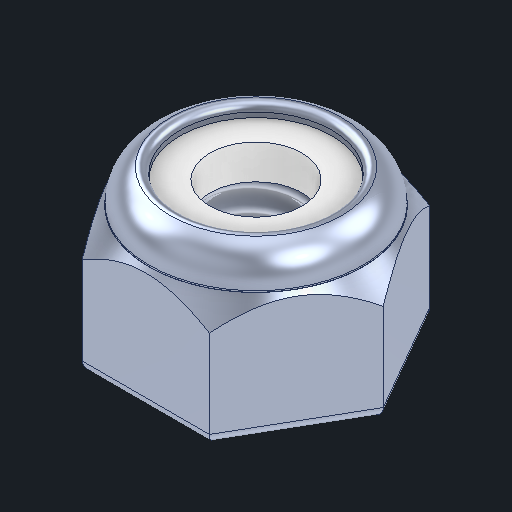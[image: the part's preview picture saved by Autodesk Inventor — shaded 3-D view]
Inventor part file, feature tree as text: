
AUTODESK INVENTOR PART (.ipt)
format: ipt  version: 2024 (Build 280153000, 153)  size: 225,792 bytes
history: native  units: in
note: dims shown in document units (in); Inventor stores cm internally (conversion verified against a paired STEP export)
features: other x4, plane x2, sketch x1
ambient origin geometry x8: Origin, YZ Plane, XZ Plane, XY Plane, X Axis, Y Axis, Z Axis, Center Point
bodies: Body1 (feature_tree)
feature tree (7):
  other  "Nut Nylock.ipt"
  other  "NONE::Nut Nylock.ipt"
  other  "TaggingFeature1"
  sketch  "Sketch1"  dims[d0=0.3937in]
  plane  "Work Plane1"
  plane  "Work Plane2"
  parser-record x1  (decoder bookkeeping rows leaked as tree rows — omitted from the tree; the rows remain in map.json)
